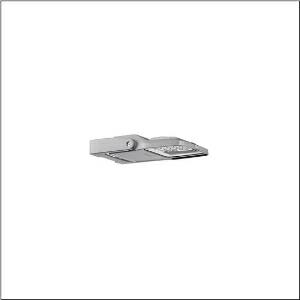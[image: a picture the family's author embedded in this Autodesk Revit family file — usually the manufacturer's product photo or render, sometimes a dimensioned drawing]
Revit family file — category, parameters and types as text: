
# Revit family: floodlight_fl_21_iq_micro___pl43_5xa7761a4a2a_9599
name_source: partatom
category: Lighting Fixtures
units: mm (PartAtom-declared; Revit-internal decimal feet)

## family parameters
Cut with Voids When Loaded = No
Host = Face
Light Source = No
Part Type = Normal
Room Calculation Point = No
Round Connector Dimension = Use Diameter
Shared = No

## types (1)
- --- (1 x LED, 3170 lm, 23.1 W, 4000K)
    Apparent Load = 23 VA
    CIE Flux Codes = 29 80 99 100 100
    Color Rendering = 70
    Color Temperature = 4000K
    Default Elevation = 1800 mm
    Description = Floodlight FL 21 iQ micro, floodlight, primary light control with lens, of PMMA, primary optical cover: protective disc, of toughened safety glass, transparent, light distribution: PL43, light emission: direct distribution, installation type: surface-mounted, LED, High Power LED, rated luminous flux: 3.170lm, luminous efficacy: 137lm/W, light colour: 740, colour temperature: 4000K, control gear: iQ Comfort/DALI, control: optimised constant luminous flux control (CLO 2.0), Desk-Remote (wireless, voltage-free reading and setting of iQ features in the workshop via application-optimized NFC function/RFID function), Light-Fading, Smart-Wire, Night-Set, Lumen-Switch, Temp-Guard, Auto-Match, with terminal, 6-pole, mains connection: 220..240V, AC, 50/60Hz, start of lifetime: 23W, end of service life: 24W, reduction: 11W, luminaire housing, of diecast aluminium, powder-coated, Siteco® metallic grey (DB 702S), corrosivity category C5 mid according to DIN EN ISO 12944, suitable for swimming pools, chlorine-resistant, sealing non-destructively replaceable, design bracket, of diecast aluminium, powder-coated, Siteco® metallic grey (DB 702S), protection rating (complete): IP66, insulation class (complete): insulation class II (safety insulation), certification: CE, ENEC, VDE, protection symbol: D, impact resistance: IK07, permissible operating ambient temperature: -40..+40°C, permissible operating ambient temperature for outdoor applications: -40..+50°C, standard: DIN EN 12944, LABS conformity tested according to VDMA 24364:2018-05, packaging unit: 1 piece

Light Distribution: PL43
    Height = 65 mm
    Lamp = 1 x LED
    Lamp Light Flux = 3170 lm
    Lamp Power = 23.1 W
    Lamp count = 1
    Length = 312 mm
    Luminous efficacy = 137 lm/W
    Manufacturer = Siteco
    ModVariant = No
    Model = 5XA7761A4A2A
    Mounting Place = Wall
    Mounting Type = Surface mounted
    Number of Poles = 1
    OnlyDefault = Yes
    Power Factor = 1
    Product Name = Floodlight FL 21 iQ micro | PL43
    Product group = floodlight | wall mounted
    ProductGroupID = 2001
    Protection Class = Protection class II
    Protection Degree = IP 66
    RLX_Detail_Level = 1
    RLX_Emergency_Light_Flux = 0 lm
    RLX_Emergency_Type = 0
    RLX_Emergency_Type_DB = No
    RlxData = <blob elided: 97393 chars, md5=81341622>
    Socket = socket
    Standby Power = 0 W
    System Light Flux = 3170 lm
    System Power = 23 W
    Type Comments = factory setting: luminous flux: 100 % | dim-lin: 254 | 455 mA
    Type Image = l_1006878.jpg
    URL = http://relux.com
    VarID = @adj_176756
    Voltage = 0 V
    Weight = 0.00 kg
    Width = 230 mm

## geometry (parser evidence)
native form markers: Blend x4, Sweep x11
no freeform markers — native parametric forms only
